# Revit family: Robinet mitigeur temporisé pour lavabo- PRESTO 4000 S-28610
name_source: partatom
category: Plumbing Fixtures
revit_build: Autodesk Revit MEP 2014 (Build: 20131024_2115(x64)
units: mm (PartAtom-declared; Revit-internal decimal feet)

## types (1)
- Robinet mitigeur temporisé pour lavabo- PRESTO 4000 S-28610
    BIMobject category = Sanitary
    CW Inlet = 10 mm  [stored 0.0328084 ft]
    Date of publishing = 2011-07-27
    Default Elevation = 1219 mm
    Description = PRESTO 4000 S single control mixer tap
    Design country = France
    Durée d'écoulement (± 5 secondes) = 15.0 s
    Débit = 180.0 L/s
    Edition number = 1
    HW Inlet = 10 mm  [stored 0.0328084 ft]
    Height = 145 mm  [stored 0.475722 ft]
    IFC Classification = Space Heater
    Manufacturer = PRESTO LES ROBINETS
    Manufacturer country = France
    Manufacturer name = Presto
    Material main = Chrome
    Material secondary = Chrome
    Model = 28610
    Nominal height = 145.00
    Nominal width = 123.00
    Pression d'utilisation recommandée = 1 à 5 bars
    Product Guid = 462c7c62-52df-4fe3-acff-f39f231f0563
    Product SKU = 28610
    Product data url = http://bimobject.com
    Product family = Mixer Tap
    Product group = Deck-mounted
    QR code = http://bimobject.com
    Résistance thermique (30 minutes) = 75 °C
    UNSPSC Code = 301815
    URL to Data = http://www.prestodatashare.com
    Warranty = 10
    Weight Net (Kg) = 0
    Width = 123 mm  [stored 0.403543 ft]

note: [stored X ft] marks values corroborated as IEEE doubles in the binary element streams (Revit-internal decimal feet)

## geometry (parser evidence)
native form markers: Sweep x8
no freeform markers — native parametric forms only
